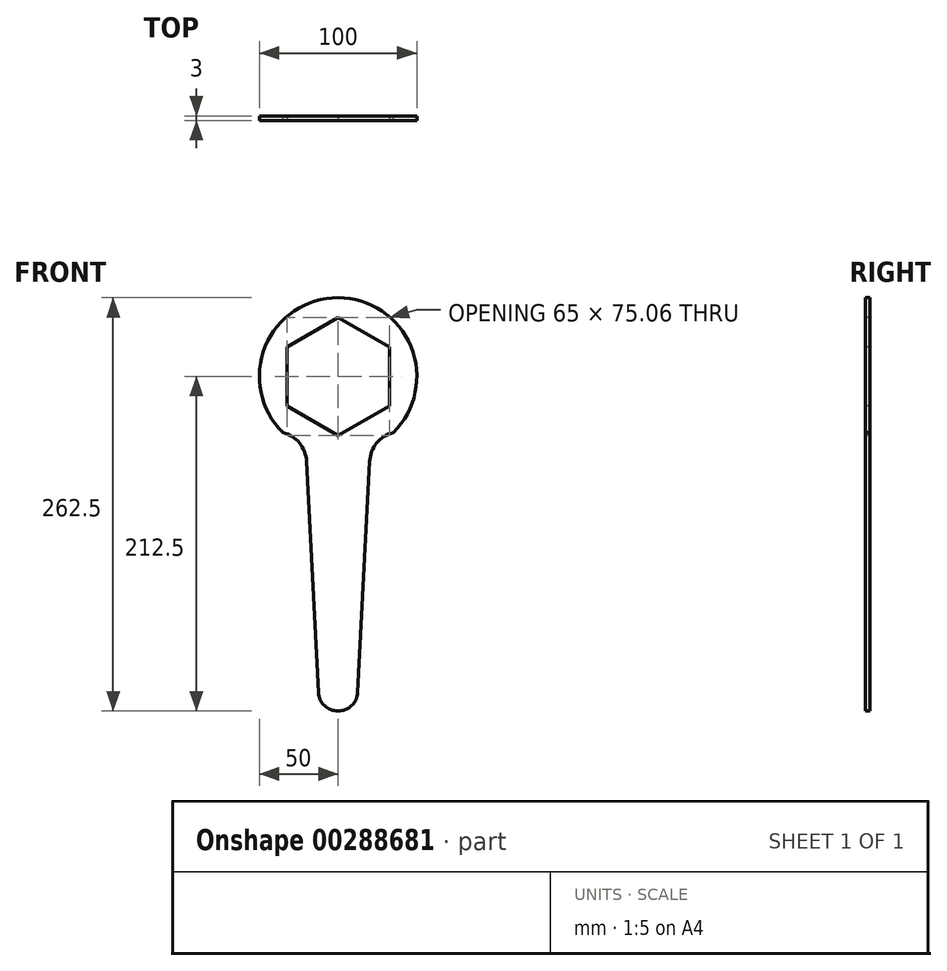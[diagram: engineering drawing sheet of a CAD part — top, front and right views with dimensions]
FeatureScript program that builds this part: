
annotation { "Feature Type Name" : "Feature", "Feature Type Description" : "" }
export const myFeature = defineFeature(function(context is Context, id is Id, definition is map)
    precondition{}
    {
        {
            var Q0;
            Q0=qCreatedBy(makeId("Front.planeOp"),FACE);
            var sketch = newSketch(context, id + "F0", { "sketchPlane" : qUnion([Q0])});
            skArc(sketch, "E0", {"start": v(35.1, -35.6) * mm, "mid": v(0, 50) * mm, "end": v(-35.1, -35.6) * mm});
            skPoint(sketch, "E1", {"position": v(0, -200) * mm});
            skPoint(sketch, "E2", {"position": v(-40, -55) * mm});
            skArc(sketch, "E3", {"start": v(-20.03, -53.97) * mm, "mid": v(-24.54, -42.31) * mm, "end": v(-35.1, -35.6) * mm});
            skArc(sketch, "E4", {"start": v(-12.48, -200.64) * mm, "mid": v(0, -212.5) * mm, "end": v(12.48, -200.64) * mm});
            skLineSegment(sketch, "E5", {"start": v(-12.48, -200.64) * mm, "end": v(-20.03, -53.97) * mm});
            skPoint(sketch, "E6", {"position": v(40, -55) * mm});
            skArc(sketch, "E7", {"start": v(35.1, -35.6) * mm, "mid": v(24.54, -42.31) * mm, "end": v(20.03, -53.97) * mm});
            skLineSegment(sketch, "E8", {"start": v(12.48, -200.64) * mm, "end": v(20.03, -53.97) * mm});
            skSolve(sketch);
        }
        {
            var Q0;
            Q0=makeQuery(id+"F0.imprint","IMPRINT",FACE,{"disambiguationData":[TD([[makeQuery(id+"F0.imprint","IMPRINT",EDGE,{"derivedFrom":sQuery(id+"F0.wireOp",EDGE,"E0")}),1.0]])]});
            extrude(context, id + "F1", {"entities" : qUnion([Q0]), "depth" : 3 * mm});
        }
        {
            var Q0;
            Q0=makeQuery(id+"F1.opExtrude","CAP_FACE",FACE,{"disambiguationData":[OSD([sQuery(id+"F0.wireOp",EDGE,"E0"),sQuery(id+"F0.wireOp",EDGE,"E3"),sQuery(id+"F0.wireOp",EDGE,"E4"),sQuery(id+"F0.wireOp",EDGE,"E5"),sQuery(id+"F0.wireOp",EDGE,"E7"),sQuery(id+"F0.wireOp",EDGE,"E8")])],"isStart":false});
            var sketch = newSketch(context, id + "F2", { "sketchPlane" : qUnion([Q0])});
            skCircle(sketch, "E9.cCircle", {"center": v(0, 0) * mm, "radius": 32.5 * mm, "construction": true});
            skLineSegment(sketch, "E9.0", {"start": v(-32.5, -18.76) * mm, "end": v(-32.5, 18.76) * mm});
            skLineSegment(sketch, "E9.1", {"start": v(-32.5, 18.76) * mm, "end": v(0, 37.53) * mm});
            skLineSegment(sketch, "E9.2", {"start": v(0, 37.53) * mm, "end": v(32.5, 18.76) * mm});
            skLineSegment(sketch, "E9.3", {"start": v(32.5, 18.76) * mm, "end": v(32.5, -18.76) * mm});
            skLineSegment(sketch, "E9.4", {"start": v(32.5, -18.76) * mm, "end": v(0, -37.53) * mm});
            skLineSegment(sketch, "E9.5", {"start": v(0, -37.53) * mm, "end": v(-32.5, -18.76) * mm});
            skPoint(sketch, "E9.0.midPoint", {"position": v(-32.5, 0) * mm});
            skSolve(sketch);
        }
        {
            var Q0;
            Q0=makeQuery(id+"F2.imprint","IMPRINT",FACE,{"disambiguationData":[TD([[makeQuery(id+"F2.imprint","IMPRINT",EDGE,{"derivedFrom":sQuery(id+"F2.wireOp",EDGE,"E9.0")}),-1.0]])]});
            extrude(context, id + "F3", {"entities" : qUnion([Q0]), "operationType" : NewBodyOperationType.REMOVE, "oppositeDirection" : true, "depth" : 25 * mm});
        }
    });
